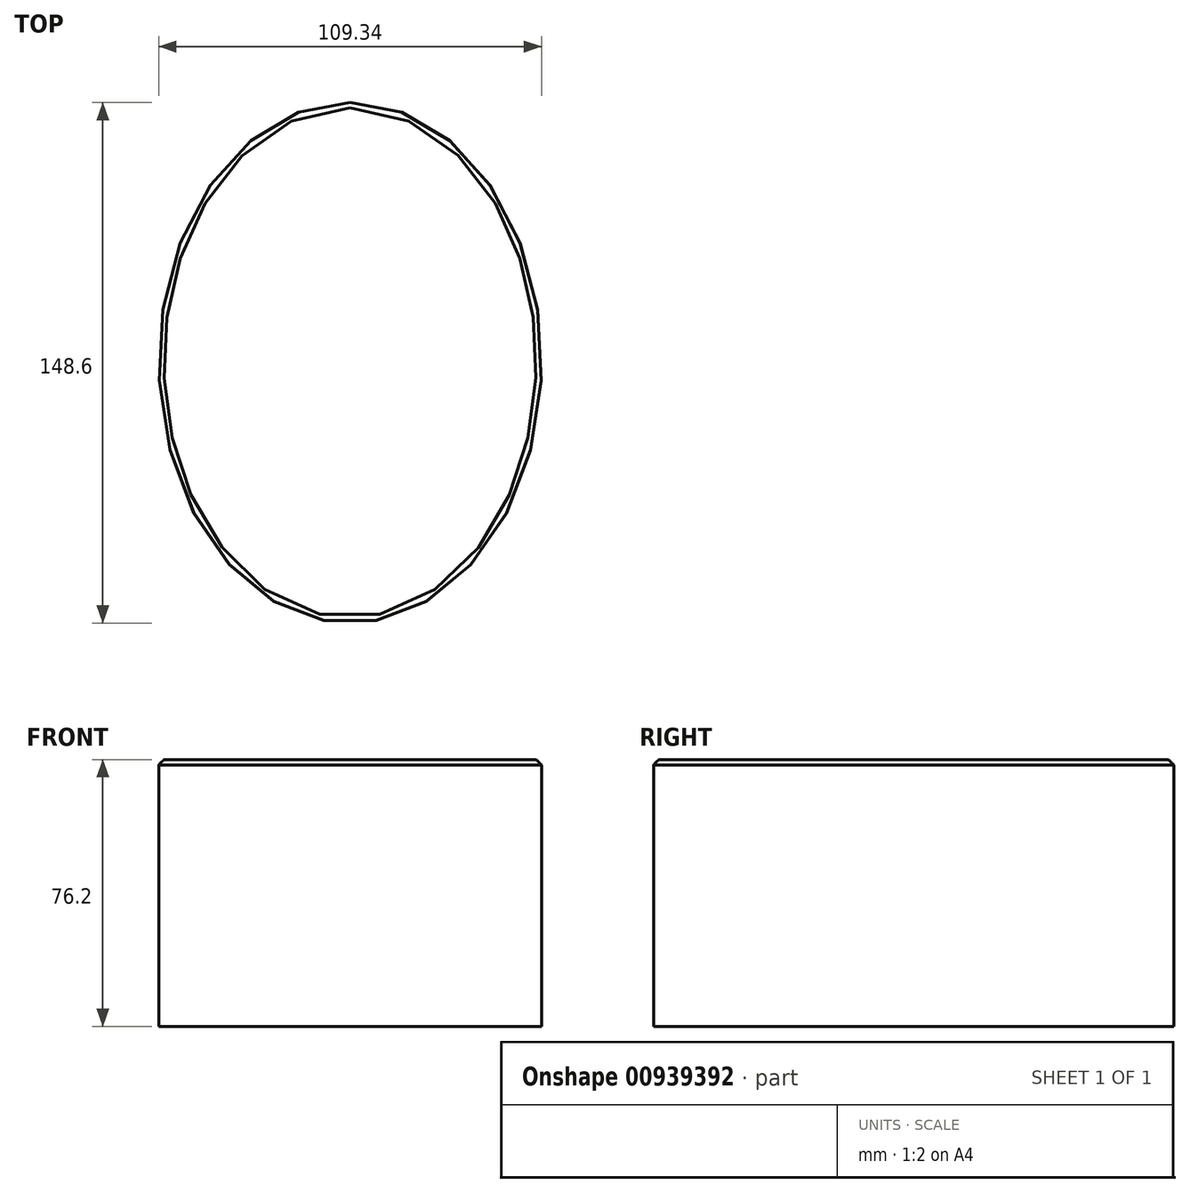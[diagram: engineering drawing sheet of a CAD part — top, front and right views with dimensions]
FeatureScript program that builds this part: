
annotation { "Feature Type Name" : "Feature", "Feature Type Description" : "" }
export const myFeature = defineFeature(function(context is Context, id is Id, definition is map)
    precondition{}
    {
        {
            var Q0;
            Q0=qCreatedBy(makeId("Top.planeOp"),FACE);
            var sketch = newSketch(context, id + "F0", { "sketchPlane" : qUnion([Q0])});
            skEllipse(sketch, "E0", {"center": v(0, 0) * mm, "majorRadius": 74.3 * mm, "minorRadius": 54.67 * mm, "majorAxis": v(0, 1)});
            skSolve(sketch);
        }
        {
            var Q0;
            Q0 = qSketchRegion(id + "F0", true);
            extrude(context, id + "F1", {"entities" : qUnion([Q0]), "oppositeDirection" : true, "depth" : 76.2 * mm, "offsetDistance" : 25.4 * mm});
        }
        {
            var Q0;
            Q0=makeQuery(id+"F1.opExtrude","CAP_EDGE",EDGE,{"disambiguationData":[OSD([sQuery(id+"F0.wireOp",EDGE,"E0")])],"isStart":true});
            chamfer(context, id + "F2", {"entities" : qUnion([Q0]), "width" : 1.52 * mm, "tangentPropagation" : true});
        }
        {
            var Q0;
            Q0=qCreatedBy(makeId("Top.planeOp"),FACE);
            var sketch = newSketch(context, id + "F3", { "sketchPlane" : qUnion([Q0])});
            skText(sketch, "E1", { "text": "Beast", "fontName": "AllertaStencil-Regular.ttf"});
            const initialGuessF3  = {"E1": [-0.02398, 0.04297, 1, 0, 0.01313]};
            skSetInitialGuess(sketch, initialGuessF3);
            skSolve(sketch);
        }
        {
            var Q0;
            Q0 = qSketchRegion(id + "F3", true);
            var Q1;
            Q1 = qBodyType(qCreatedBy(id + "F3" ,EDGE), BodyType.WIRE);
            extrude(context, id + "F4", {"entities" : qUnion([Q0]), "bodyType" : ToolBodyType.SURFACE, "surfaceEntities" : qUnion([Q1]), "oppositeDirection" : true, "depth" : 25.4 * mm, "offsetDistance" : 25.4 * mm});
        }
    });
